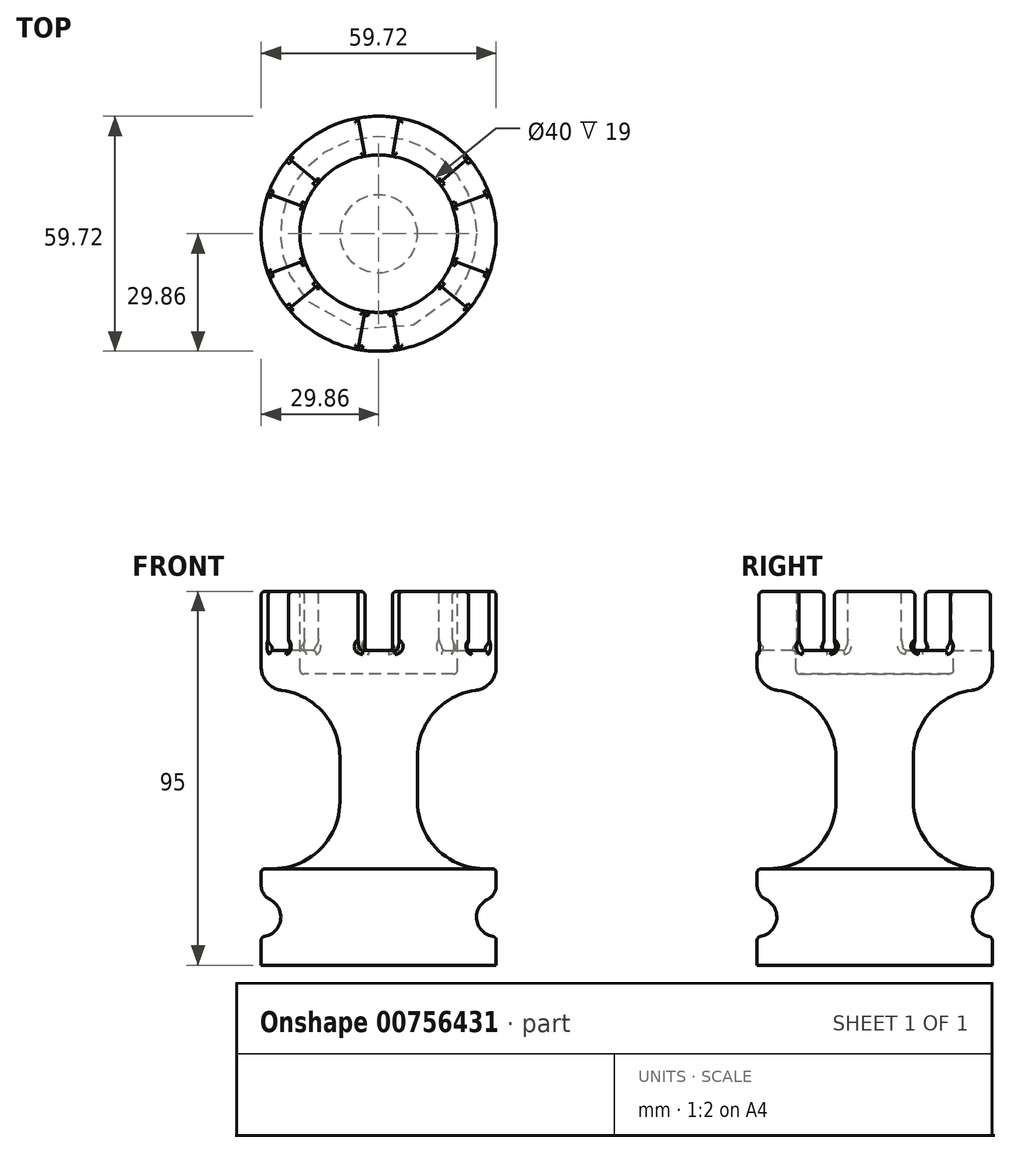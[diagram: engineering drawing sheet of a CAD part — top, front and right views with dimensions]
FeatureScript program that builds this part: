
annotation { "Feature Type Name" : "Feature", "Feature Type Description" : "" }
export const myFeature = defineFeature(function(context is Context, id is Id, definition is map)
    precondition{}
    {
        {
            var Q0;
            Q0=qCreatedBy(makeId("Front.planeOp"),FACE);
            var sketch = newSketch(context, id + "F0", { "sketchPlane" : qUnion([Q0])});
            skLineSegment(sketch, "E0.top", {"start": v(9.86, 24.52) * mm, "end": v(29.86, 24.52) * mm});
            skLineSegment(sketch, "E0.right", {"start": v(29.86, 0) * mm, "end": v(29.86, 7.26) * mm});
            skLineSegment(sketch, "E1.right", {"start": v(9.86, 24.52) * mm, "end": v(9.86, 70) * mm});
            skLineSegment(sketch, "E2.bottom", {"start": v(9.86, 70) * mm, "end": v(29.86, 70) * mm});
            skLineSegment(sketch, "E2.top", {"start": v(0, 95) * mm, "end": v(29.86, 95) * mm});
            skLineSegment(sketch, "E2.right", {"start": v(29.86, 70) * mm, "end": v(29.86, 95) * mm});
            skLineSegment(sketch, "E3", {"start": v(0, 95) * mm, "end": v(0, 0) * mm});
            skLineSegment(sketch, "E4", {"start": v(0, 0) * mm, "end": v(29.86, 0) * mm});
            skArc(sketch, "E5", {"start": v(29.86, 17.26) * mm, "mid": v(24.86, 12.26) * mm, "end": v(29.86, 7.26) * mm});
            skLineSegment(sketch, "E6.trimOffspring", {"start": v(29.86, 17.26) * mm, "end": v(29.86, 24.52) * mm});
            skSolve(sketch);
        }
        {
            var Q0;
            Q0 = qSketchRegion(id + "F0", true);
            var Q1;
            Q1=sQuery(id+"F0.wireOp",EDGE,"E3");
            revolve(context, id + "F1", {"surfaceOperationType" : NewSurfaceOperationType.NEW, "entities" : qUnion([Q0]), "axis" : qUnion([Q1]), "revolveType" : RevolveType.FULL});
        }
        {
            var Q0;
            Q0=makeQuery(id+"F1.opRevolve","SWEPT_FACE",FACE,{"disambiguationData":[OSD([sQuery(id+"F0.wireOp",EDGE,"E2.top")])]});
            var sketch = newSketch(context, id + "F2", { "sketchPlane" : qUnion([Q0])});
            skCircle(sketch, "E7", {"center": v(0, 0) * mm, "radius": 20 * mm});
            skSolve(sketch);
        }
        {
            var Q0;
            Q0=qSketchRegion(id+"F2",true);
            extrude(context, id + "F3", {"entities" : qUnion([Q0]), "operationType" : NewBodyOperationType.REMOVE, "oppositeDirection" : true, "depth" : 21 * mm, "offsetDistance" : 25 * mm});
        }
        {
            var Q0;
            Q0=makeQuery(id+"F1.opRevolve","SWEPT_FACE",FACE,{"disambiguationData":[OSD([sQuery(id+"F0.wireOp",EDGE,"E2.top")])]});
            var sketch = newSketch(context, id + "F4", { "sketchPlane" : qUnion([Q0])});
            skLineSegment(sketch, "E8", {"start": v(3.47, 19.7) * mm, "end": v(5.2, 29.54) * mm});
            skLineSegment(sketch, "E9", {"start": v(-3.47, 19.7) * mm, "end": v(-5.2, 29.54) * mm});
            skArc(sketch, "E10", {"start": v(5.2, 29.54) * mm, "mid": v(0, 30) * mm, "end": v(-5.2, 29.54) * mm});
            skArc(sketch, "E11", {"start": v(3.47, 19.7) * mm, "mid": v(0, 20) * mm, "end": v(-3.47, 19.7) * mm});
            skLineSegment(sketch, "E12.1.0", {"start": v(-18.8, 6.84) * mm, "end": v(-28.2, 10.26) * mm});
            skArc(sketch, "E12.1.1", {"start": v(-15.32, 12.86) * mm, "mid": v(-17.32, 10) * mm, "end": v(-18.8, 6.84) * mm});
            skLineSegment(sketch, "E12.1.2", {"start": v(-15.32, 12.86) * mm, "end": v(-22.98, 19.28) * mm});
            skArc(sketch, "E12.1.3", {"start": v(-22.98, 19.28) * mm, "mid": v(-25.98, 15) * mm, "end": v(-28.2, 10.26) * mm});
            skLineSegment(sketch, "E12.2.0", {"start": v(-15.32, -12.86) * mm, "end": v(-22.98, -19.28) * mm});
            skArc(sketch, "E12.2.1", {"start": v(-18.8, -6.84) * mm, "mid": v(-17.32, -10) * mm, "end": v(-15.32, -12.86) * mm});
            skLineSegment(sketch, "E12.2.2", {"start": v(-18.8, -6.84) * mm, "end": v(-28.2, -10.26) * mm});
            skArc(sketch, "E12.2.3", {"start": v(-28.2, -10.26) * mm, "mid": v(-25.98, -15) * mm, "end": v(-22.98, -19.28) * mm});
            skLineSegment(sketch, "E12.3.0", {"start": v(3.47, -19.7) * mm, "end": v(5.2, -29.54) * mm});
            skArc(sketch, "E12.3.1", {"start": v(-3.47, -19.7) * mm, "mid": v(0, -20) * mm, "end": v(3.47, -19.7) * mm});
            skLineSegment(sketch, "E12.3.2", {"start": v(-3.47, -19.7) * mm, "end": v(-5.2, -29.54) * mm});
            skArc(sketch, "E12.3.3", {"start": v(-5.2, -29.54) * mm, "mid": v(0, -30) * mm, "end": v(5.2, -29.54) * mm});
            skLineSegment(sketch, "E12.4.0", {"start": v(18.8, -6.84) * mm, "end": v(28.2, -10.26) * mm});
            skArc(sketch, "E12.4.1", {"start": v(15.32, -12.86) * mm, "mid": v(17.32, -10) * mm, "end": v(18.8, -6.84) * mm});
            skLineSegment(sketch, "E12.4.2", {"start": v(15.32, -12.86) * mm, "end": v(22.98, -19.28) * mm});
            skArc(sketch, "E12.4.3", {"start": v(22.98, -19.28) * mm, "mid": v(25.98, -15) * mm, "end": v(28.2, -10.26) * mm});
            skLineSegment(sketch, "E12.5.0", {"start": v(15.32, 12.86) * mm, "end": v(22.98, 19.28) * mm});
            skArc(sketch, "E12.5.1", {"start": v(18.8, 6.84) * mm, "mid": v(17.32, 10) * mm, "end": v(15.32, 12.86) * mm});
            skLineSegment(sketch, "E12.5.2", {"start": v(18.8, 6.84) * mm, "end": v(28.2, 10.26) * mm});
            skArc(sketch, "E12.5.3", {"start": v(28.2, 10.26) * mm, "mid": v(25.98, 15) * mm, "end": v(22.98, 19.28) * mm});
            skSolve(sketch);
        }
        {
            var Q0;
            Q0=qSketchRegion(id+"F4",true);
            extrude(context, id + "F5", {"entities" : qUnion([Q0]), "operationType" : NewBodyOperationType.REMOVE, "oppositeDirection" : true, "depth" : 15 * mm, "offsetDistance" : 25 * mm});
        }
        {
            var Q0;
            Q0=makeQuery(id+"F1.opRevolve","SWEPT_FACE",FACE,{"disambiguationData":[OSD([sQuery(id+"F0.wireOp",EDGE,"E1.right")])]});
            fillet(context, id + "F6", {"entities" : qUnion([Q0]), "radius" : 17 * mm, "tangentPropagation" : true, "allowEdgeOverflow" : false});
        }
        {
            var Q0;
            Q0=makeQuery(id+"F1.opRevolve","SWEPT_EDGE",EDGE,{"disambiguationData":[OSD([sQuery(id+"F0.wireOp",EDGE,"E2.bottom"),sQuery(id+"F0.wireOp",EDGE,"E2.right")])]});
            fillet(context, id + "F7", {"entities" : qUnion([Q0]), "radius" : 6 * mm, "tangentPropagation" : true, "allowEdgeOverflow" : false});
        }
        {
            var Q0;
            Q0=makeQuery(id+"F1.opRevolve","SWEPT_EDGE",EDGE,{"disambiguationData":[OSD([sQuery(id+"F0.wireOp",EDGE,"E0.top"),sQuery(id+"F0.wireOp",EDGE,"E6.trimOffspring")])]});
            var Q1;
            Q1=makeQuery(id+"F5.boolean.opBoolean","SPLIT",FACE,{"disambiguationData":[TD([makeQuery(id+"F5.opExtrude","SWEPT_FACE",FACE,{"disambiguationData":[OSD([sQuery(id+"F4.wireOp",EDGE,"E12.3.0")])]})])],"derivedFrom":makeQuery(id+"F1.opRevolve","SWEPT_FACE",FACE,{"disambiguationData":[OSD([sQuery(id+"F0.wireOp",EDGE,"E2.top")])]})});
            var Q2;
            Q2=makeQuery(id+"F5.boolean.opBoolean","SPLIT",FACE,{"disambiguationData":[TD([makeQuery(id+"F5.opExtrude","SWEPT_FACE",FACE,{"disambiguationData":[OSD([sQuery(id+"F4.wireOp",EDGE,"E12.4.0")])]})])],"derivedFrom":makeQuery(id+"F1.opRevolve","SWEPT_FACE",FACE,{"disambiguationData":[OSD([sQuery(id+"F0.wireOp",EDGE,"E2.top")])]})});
            var Q3;
            Q3=makeQuery(id+"F5.boolean.opBoolean","SPLIT",FACE,{"disambiguationData":[TD([makeQuery(id+"F5.opExtrude","SWEPT_FACE",FACE,{"disambiguationData":[OSD([sQuery(id+"F4.wireOp",EDGE,"E8")])]})])],"derivedFrom":makeQuery(id+"F1.opRevolve","SWEPT_FACE",FACE,{"disambiguationData":[OSD([sQuery(id+"F0.wireOp",EDGE,"E2.top")])]})});
            var Q4;
            Q4=makeQuery(id+"F5.boolean.opBoolean","SPLIT",FACE,{"disambiguationData":[TD([makeQuery(id+"F5.opExtrude","SWEPT_FACE",FACE,{"disambiguationData":[OSD([sQuery(id+"F4.wireOp",EDGE,"E9")])]})])],"derivedFrom":makeQuery(id+"F1.opRevolve","SWEPT_FACE",FACE,{"disambiguationData":[OSD([sQuery(id+"F0.wireOp",EDGE,"E2.top")])]})});
            var Q5;
            Q5=makeQuery(id+"F5.boolean.opBoolean","SPLIT",FACE,{"disambiguationData":[TD([makeQuery(id+"F5.opExtrude","SWEPT_FACE",FACE,{"disambiguationData":[OSD([sQuery(id+"F4.wireOp",EDGE,"E12.1.0")])]})])],"derivedFrom":makeQuery(id+"F1.opRevolve","SWEPT_FACE",FACE,{"disambiguationData":[OSD([sQuery(id+"F0.wireOp",EDGE,"E2.top")])]})});
            var Q6;
            Q6=makeQuery(id+"F5.boolean.opBoolean","SPLIT",FACE,{"disambiguationData":[TD([makeQuery(id+"F5.opExtrude","SWEPT_FACE",FACE,{"disambiguationData":[OSD([sQuery(id+"F4.wireOp",EDGE,"E12.2.0")])]})])],"derivedFrom":makeQuery(id+"F1.opRevolve","SWEPT_FACE",FACE,{"disambiguationData":[OSD([sQuery(id+"F0.wireOp",EDGE,"E2.top")])]})});
            var Q7;
            Q7=makeQuery(id+"F3.boolean.opBoolean","COPY",EDGE,{"derivedFrom":makeQuery(id+"F3.opExtrude","CAP_EDGE",EDGE,{"disambiguationData":[OSD([sQuery(id+"F2.wireOp",EDGE,"E7")])],"isStart":false})});
            var Q8;
            Q8=makeQuery(id+"F5.boolean.opBoolean","COPY",FACE,{"derivedFrom":makeQuery(id+"F5.opExtrude","CAP_FACE",FACE,{"disambiguationData":[OSD([sQuery(id+"F4.wireOp",EDGE,"E12.1.0"),sQuery(id+"F4.wireOp",EDGE,"E12.1.1"),sQuery(id+"F4.wireOp",EDGE,"E12.1.2"),sQuery(id+"F4.wireOp",EDGE,"E12.1.3")])],"isStart":false})});
            var Q9;
            Q9=makeQuery(id+"F5.boolean.opBoolean","COPY",EDGE,{"derivedFrom":makeQuery(id+"F5.opExtrude","CAP_EDGE",EDGE,{"disambiguationData":[OSD([sQuery(id+"F4.wireOp",EDGE,"E11")])],"isStart":false})});
            var Q10;
            Q10=makeQuery(id+"F5.boolean.opBoolean","INTERSECT",EDGE,{"derivedFrom":[makeQuery(id+"F1.opRevolve","SWEPT_FACE",FACE,{"disambiguationData":[OSD([sQuery(id+"F0.wireOp",EDGE,"E2.right")])]}),makeQuery(id+"F5.opExtrude","CAP_FACE",FACE,{"disambiguationData":[OSD([sQuery(id+"F4.wireOp",EDGE,"E12.5.0"),sQuery(id+"F4.wireOp",EDGE,"E12.5.1"),sQuery(id+"F4.wireOp",EDGE,"E12.5.2"),sQuery(id+"F4.wireOp",EDGE,"E12.5.3")])],"isStart":false})]});
            var Q11;
            Q11=makeQuery(id+"F5.boolean.opBoolean","COPY",FACE,{"derivedFrom":makeQuery(id+"F5.opExtrude","CAP_FACE",FACE,{"disambiguationData":[OSD([sQuery(id+"F4.wireOp",EDGE,"E12.4.0"),sQuery(id+"F4.wireOp",EDGE,"E12.4.1"),sQuery(id+"F4.wireOp",EDGE,"E12.4.2"),sQuery(id+"F4.wireOp",EDGE,"E12.4.3")])],"isStart":false})});
            var Q12;
            Q12=makeQuery(id+"F5.boolean.opBoolean","COPY",FACE,{"derivedFrom":makeQuery(id+"F5.opExtrude","CAP_FACE",FACE,{"disambiguationData":[OSD([sQuery(id+"F4.wireOp",EDGE,"E12.3.0"),sQuery(id+"F4.wireOp",EDGE,"E12.3.1"),sQuery(id+"F4.wireOp",EDGE,"E12.3.2"),sQuery(id+"F4.wireOp",EDGE,"E12.3.3")])],"isStart":false})});
            var Q13;
            Q13=makeQuery(id+"F5.boolean.opBoolean","COPY",FACE,{"derivedFrom":makeQuery(id+"F5.opExtrude","CAP_FACE",FACE,{"disambiguationData":[OSD([sQuery(id+"F4.wireOp",EDGE,"E12.2.0"),sQuery(id+"F4.wireOp",EDGE,"E12.2.1"),sQuery(id+"F4.wireOp",EDGE,"E12.2.2"),sQuery(id+"F4.wireOp",EDGE,"E12.2.3")])],"isStart":false})});
            var Q14;
            Q14=makeQuery(id+"F5.boolean.opBoolean","COPY",FACE,{"derivedFrom":makeQuery(id+"F5.opExtrude","CAP_FACE",FACE,{"disambiguationData":[OSD([sQuery(id+"F4.wireOp",EDGE,"E12.5.0"),sQuery(id+"F4.wireOp",EDGE,"E12.5.1"),sQuery(id+"F4.wireOp",EDGE,"E12.5.2"),sQuery(id+"F4.wireOp",EDGE,"E12.5.3")])],"isStart":false})});
            fillet(context, id + "F8", {"entities" : qUnion([Q0, Q1, Q2, Q3, Q4, Q5, Q6, Q7, Q8, Q9, Q10, Q11, Q12, Q13, Q14]), "radius" : 1 * mm, "tangentPropagation" : true, "allowEdgeOverflow" : false});
        }
        {
            var Q0;
            Q0=makeQuery(id+"F1.opRevolve","SWEPT_EDGE",EDGE,{"disambiguationData":[OSD([sQuery(id+"F0.wireOp",EDGE,"E0.right"),sQuery(id+"F0.wireOp",EDGE,"E5")])]});
            fillet(context, id + "F9", {"entities" : qUnion([Q0]), "radius" : 1 * mm, "tangentPropagation" : true, "allowEdgeOverflow" : false});
        }
        {
            var Q0;
            Q0=makeQuery(id+"F1.opRevolve","SWEPT_EDGE",EDGE,{"disambiguationData":[OSD([sQuery(id+"F0.wireOp",EDGE,"E5"),sQuery(id+"F0.wireOp",EDGE,"E6.trimOffspring")])]});
            fillet(context, id + "F10", {"entities" : qUnion([Q0]), "radius" : 4 * mm, "tangentPropagation" : true, "allowEdgeOverflow" : false});
        }
    });
